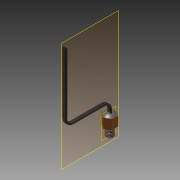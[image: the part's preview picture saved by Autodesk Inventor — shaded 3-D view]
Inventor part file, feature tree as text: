
AUTODESK INVENTOR PART (.ipt)
format: ipt  version: 2015 (Build 190159000, 159)  size: 135,680 bytes
history: native  units: mm
features: extrude x3, chamfer x1, thread x1, revolve x1, plane x1, sweep x1, mirror x1
ambient origin geometry x8: Origin, YZ Plane, XZ Plane, XY Plane, X Axis, Y Axis, Z Axis, Center Point
bodies: Solid1 (feature_tree)
feature tree (9):
  extrude  "Extrusión1"  Depth=4.68mm
  extrude  "Extrusión2"  Depth=4.0mm TaperAngle=0.0deg
  chamfer  "Chaflán1"  Distance=3.0mm
  extrude  "Extrusión3"  Depth=4.0mm TaperAngle=0.0deg
  thread  "Rosca1"  [1 undecoded]
  revolve  "Revolución1"  [1 undecoded]
  plane  "Plano de trabajo1"
  sweep  "Barrido1"
  mirror  "Simetría1"
note: 2 required parameter values undecoded (feature->parameter linkage not recoverable at this tier; creation-order binding heuristic only, values carry confidence <= 0.55)